# Revit family: RUFO-600-5000-830x
name_source: partatom
category: Oprawy oświetleniowe
revit_build: Autodesk Revit 2017 (Build: 20190507_1515(x64)
units: mm (PartAtom-declared; Revit-internal decimal feet)

## family parameters
Numer OmniClass = 23.80.70.11
Obiekt nadrzędny = Powierzchnia
Punkt obliczania pomieszczeń = Nie
Tnij formami wycięć po wczytaniu = Tak
Typ części = Normalny
Tytuł OmniClass = Luminaries for Internal Lighting
Współdzielony = Nie
Wymiar okrągłego złącza = Użyj średnicy
Źródło światła = Tak

## types (8) — shared parameters
Emituj kształt widoczny w renderingu = Nie
Emituj ze średnicy okręgu = 600 mm
Filtr koloru = 16777215
Kod zespołu = D5020200
Lampa = LED
Obciążenie pozorne = 37 VA
Odchylenie kierunku = 90.00°
Plik sieci fotometrycznej = RUFO 6005000-840.IES
Producent = RIDI Leuchten GmbH
URL = www.ridi.de
Zmiana temperatury barwowej przyciemniania lampy = <Brak>
brand = RIDI
conformity mark = CE
electrical safety class = 1
height = 165 mm
ingress protection (IP) code = IP20
length = 600 mm
nominal frequency = 50-60Hz
nominal voltage = 230
rated input power = 37
voltage type (AC, DC, UC) = AC
width = 600 mm
zero-valued in all types: Domyślna rzędna

## per-type parameters (varying)
| type | Model | product name | weight |
| RUFO 600/5000-830 | 0420641 | RUFO 600/5000-830 | 4.5kg |
| RUFO 600/5000-830-DALI | 0430641 | RUFO 600/5000-830 | 4.5kg |
| RUFO 600/5000-830 2K | 0420691 | RUFO 600/5000-830 2K | 4.5kg |
| RUFO 600/5000-830 2K-EDS3 | 0420691//377 | RUFO 600/5000-830 2K-EDS3 | 4.5kg |
| RUFO 600/5000-830 2K-RS | 0420691//396 | RUFO 600/5000-830 2K-RS | 4.5kg |
| RUFO 600/5000-830 2K-RS-EDS3 | 0420691//377396 | RUFO 600/5000-830 2K-RS-EDS3 | 4.5kg |
| RUFO 600/5000-830 EDS3 | 0420641//377 | RUFO 600/5000-830 EDS3 | 4.87kg |
| RUFO 600/5000-830 RS | 0420641//396 | RUFO 600/5000-830 RS | 4.5kg |
